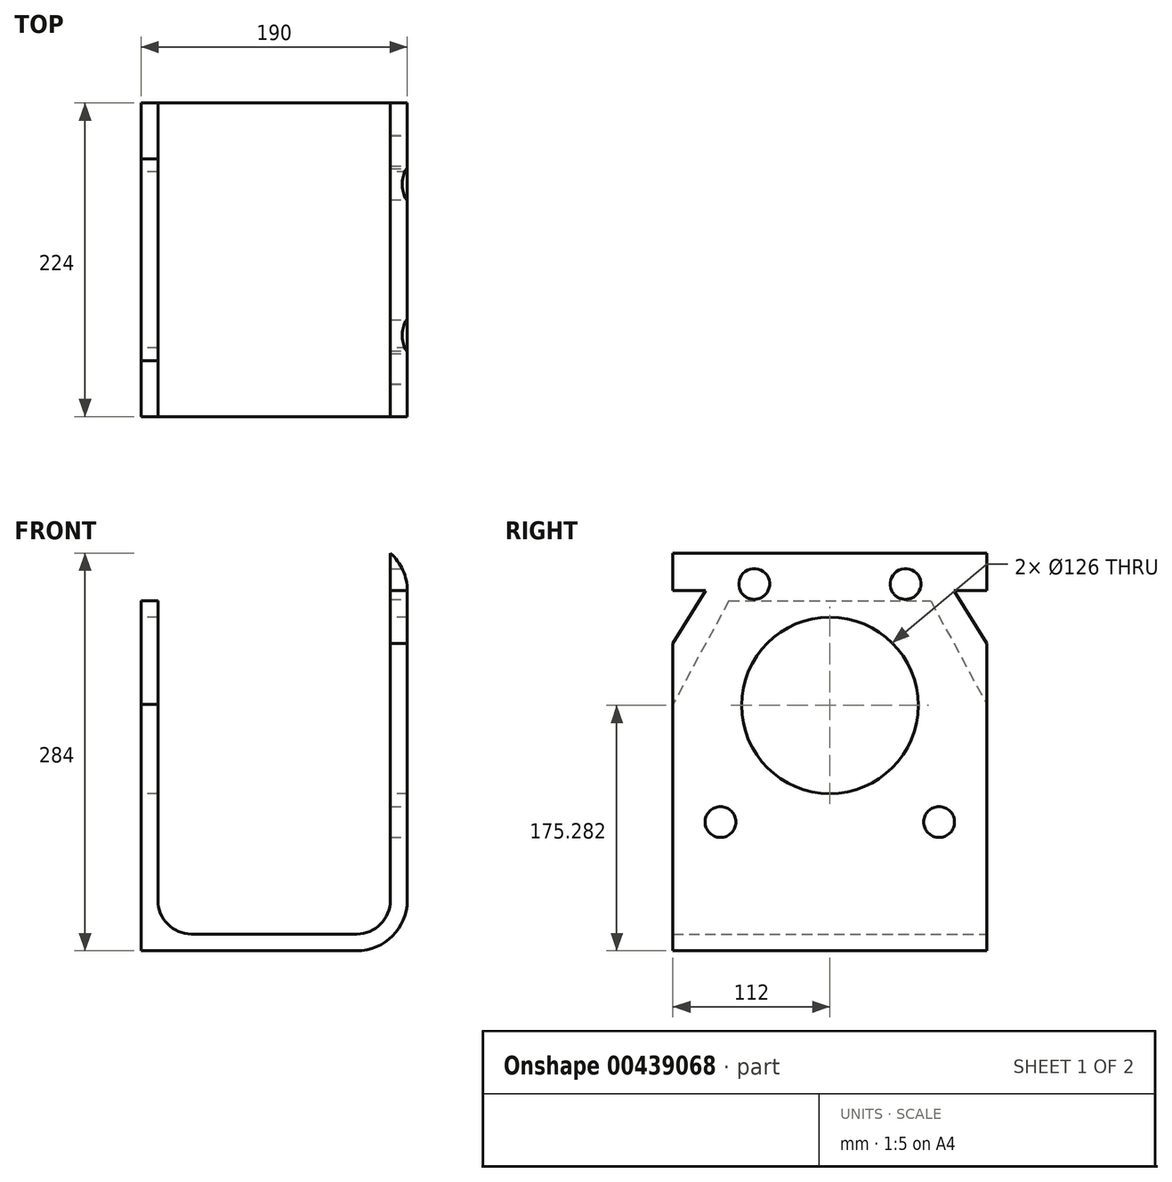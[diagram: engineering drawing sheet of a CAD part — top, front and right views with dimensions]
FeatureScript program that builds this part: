
annotation { "Feature Type Name" : "Feature", "Feature Type Description" : "" }
export const myFeature = defineFeature(function(context is Context, id is Id, definition is map)
    precondition{}
    {
        {
            var Q0;
            Q0=qCreatedBy(makeId("Front.planeOp"),FACE);
            var sketch = newSketch(context, id + "F0", { "sketchPlane" : qUnion([Q0])});
            skLineSegment(sketch, "E0.bottom", {"start": v(-35.67, 188.2) * mm, "end": v(-23.67, 188.2) * mm});
            skLineSegment(sketch, "E0.top", {"start": v(-35.67, -61.8) * mm, "end": v(-23.67, -61.8) * mm});
            skLineSegment(sketch, "E0.left", {"start": v(-35.67, 188.2) * mm, "end": v(-35.67, -61.8) * mm});
            skLineSegment(sketch, "E0.right", {"start": v(-23.67, 188.2) * mm, "end": v(-23.67, -61.8) * mm});
            skLineSegment(sketch, "E1.bottom", {"start": v(-35.67, -61.8) * mm, "end": v(154.33, -61.8) * mm});
            skLineSegment(sketch, "E1.top", {"start": v(-35.67, -49.8) * mm, "end": v(154.33, -49.8) * mm});
            skLineSegment(sketch, "E1.left", {"start": v(-35.67, -61.8) * mm, "end": v(-35.67, -49.8) * mm});
            skLineSegment(sketch, "E1.right", {"start": v(154.33, -61.8) * mm, "end": v(154.33, -49.8) * mm});
            skLineSegment(sketch, "E2.bottom", {"start": v(154.33, -61.8) * mm, "end": v(142.33, -61.8) * mm});
            skLineSegment(sketch, "E2.top", {"start": v(154.33, 222.2) * mm, "end": v(142.33, 222.2) * mm});
            skLineSegment(sketch, "E2.left", {"start": v(154.33, -61.8) * mm, "end": v(154.33, 222.2) * mm});
            skLineSegment(sketch, "E2.right", {"start": v(142.33, -61.8) * mm, "end": v(142.33, 222.2) * mm});
            skSolve(sketch);
        }
        {
            var Q0;
            Q0=qSketchRegion(id+"F0",true);
            extrude(context, id + "F1", {"entities" : qUnion([Q0]), "depth" : 224 * mm});
        }
        {
            var Q0;
            Q0=makeQuery(id+"F1.opExtrude","SWEPT_EDGE",EDGE,{"disambiguationData":[OSD([sQuery(id+"F0.wireOp",EDGE,"E0.right"),sQuery(id+"F0.wireOp",EDGE,"E1.top")])]});
            var Q1;
            Q1=makeQuery(id+"F1.opExtrude","SWEPT_EDGE",EDGE,{"disambiguationData":[OSD([sQuery(id+"F0.wireOp",EDGE,"E1.top"),sQuery(id+"F0.wireOp",EDGE,"E2.right")])]});
            fillet(context, id + "F2", {"entities" : qUnion([Q0, Q1]), "radius" : 24 * mm, "tangentPropagation" : true, "allowEdgeOverflow" : false});
        }
        {
            var Q0;
            Q0=makeQuery(id+"F1.opExtrude","SWEPT_EDGE",EDGE,{"disambiguationData":[OSD([sQuery(id+"F0.wireOp",EDGE,"E2.bottom"),sQuery(id+"F0.wireOp",EDGE,"E2.left")])]});
            var Q1;
            Q1=makeQuery(id+"F1.opExtrude","SWEPT_EDGE",EDGE,{"disambiguationData":[OSD([sQuery(id+"F0.wireOp",EDGE,"E1.bottom"),sQuery(id+"F0.wireOp",EDGE,"E1.left")])]});
            fillet(context, id + "F3", {"entities" : qUnion([Q0, Q1]), "radius" : 36 * mm, "tangentPropagation" : true, "allowEdgeOverflow" : false});
        }
        {
            var Q0;
            Q0=makeQuery(id+"F1.opExtrude","SWEPT_FACE",FACE,{"disambiguationData":[OSD([sQuery(id+"F0.wireOp",EDGE,"E0.left"),sQuery(id+"F0.wireOp",EDGE,"E1.left")])]});
            var sketch = newSketch(context, id + "F4", { "sketchPlane" : qUnion([Q0])});
            skLineSegment(sketch, "E3", {"start": v(184, 188.2) * mm, "end": v(224, 114.33) * mm});
            skLineSegment(sketch, "E4", {"start": v(40, 188.2) * mm, "end": v(0, 114.33) * mm});
            skSolve(sketch);
        }
        {
            var Q0;
            {var subQ0=sQuery(id+"F4.wireOp",EDGE,"E4");Q0=makeQuery(id+"F4.imprint","IMPRINT",FACE,{"disambiguationData":[TD([[makeQuery(id+"F4.imprint","IMPRINT",EDGE,{"derivedFrom":subQ0}),-1.0]])]});}
            var Q1;
            {var subQ0=sQuery(id+"F4.wireOp",EDGE,"E3");Q1=makeQuery(id+"F4.imprint","IMPRINT",FACE,{"disambiguationData":[TD([[makeQuery(id+"F4.imprint","IMPRINT",EDGE,{"derivedFrom":subQ0}),1.0]])]});}
            extrude(context, id + "F5", {"entities" : qUnion([Q0, Q1]), "operationType" : NewBodyOperationType.REMOVE, "oppositeDirection" : true, "depth" : 12 * mm});
        }
        {
            var Q0;
            Q0=makeQuery(id+"F1.opExtrude","SWEPT_FACE",FACE,{"disambiguationData":[OSD([sQuery(id+"F0.wireOp",EDGE,"E2.left")])]});
            var sketch = newSketch(context, id + "F6", { "sketchPlane" : qUnion([Q0])});
            skLineSegment(sketch, "E5", {"start": v(-224, 157.58) * mm, "end": v(-184, 222.2) * mm});
            skLineSegment(sketch, "E6", {"start": v(-40, 222.2) * mm, "end": v(0, 157.58) * mm});
            skSolve(sketch);
        }
        {
            var Q0;
            {var subQ0=sQuery(id+"F6.wireOp",EDGE,"E5");Q0=makeQuery(id+"F6.imprint","IMPRINT",FACE,{"disambiguationData":[TD([[makeQuery(id+"F6.imprint","IMPRINT",EDGE,{"derivedFrom":subQ0}),1.0]])]});}
            var Q1;
            {var subQ0=sQuery(id+"F6.wireOp",EDGE,"E6");Q1=makeQuery(id+"F6.imprint","IMPRINT",FACE,{"disambiguationData":[TD([[makeQuery(id+"F6.imprint","IMPRINT",EDGE,{"derivedFrom":subQ0}),1.0]])]});}
            extrude(context, id + "F7", {"entities" : qUnion([Q0, Q1]), "operationType" : NewBodyOperationType.REMOVE, "oppositeDirection" : true, "depth" : 12 * mm});
        }
        {
            var Q0;
            Q0=makeQuery(id+"F1.opExtrude","SWEPT_FACE",FACE,{"disambiguationData":[OSD([sQuery(id+"F0.wireOp",EDGE,"E0.left"),sQuery(id+"F0.wireOp",EDGE,"E1.left")])]});
            var sketch = newSketch(context, id + "F8", { "sketchPlane" : qUnion([Q0])});
            skCircle(sketch, "E7", {"center": v(112, 113.48) * mm, "radius": 63 * mm});
            skSolve(sketch);
        }
        {
            var Q0;
            Q0=qSketchRegion(id+"F8",true);
            extrude(context, id + "F9", {"entities" : qUnion([Q0]), "operationType" : NewBodyOperationType.REMOVE, "oppositeDirection" : true, "depth" : 190 * mm});
        }
        {
            var Q0;
            Q0=makeQuery(id+"F1.opExtrude","SWEPT_FACE",FACE,{"disambiguationData":[OSD([sQuery(id+"F0.wireOp",EDGE,"E2.left")])]});
            var sketch = newSketch(context, id + "F10", { "sketchPlane" : qUnion([Q0])});
            skCircle(sketch, "E8", {"center": v(-166, 200.2) * mm, "radius": 11 * mm});
            skCircle(sketch, "E9", {"center": v(-58, 200.2) * mm, "radius": 11 * mm});
            skCircle(sketch, "E10", {"center": v(-34, 30.2) * mm, "radius": 11 * mm});
            skCircle(sketch, "E11", {"center": v(-190, 30.2) * mm, "radius": 11 * mm});
            skSolve(sketch);
        }
        {
            var Q0;
            Q0=qSketchRegion(id+"F10",true);
            extrude(context, id + "F11", {"entities" : qUnion([Q0]), "operationType" : NewBodyOperationType.REMOVE, "oppositeDirection" : true, "depth" : 25 * mm});
        }
    });
